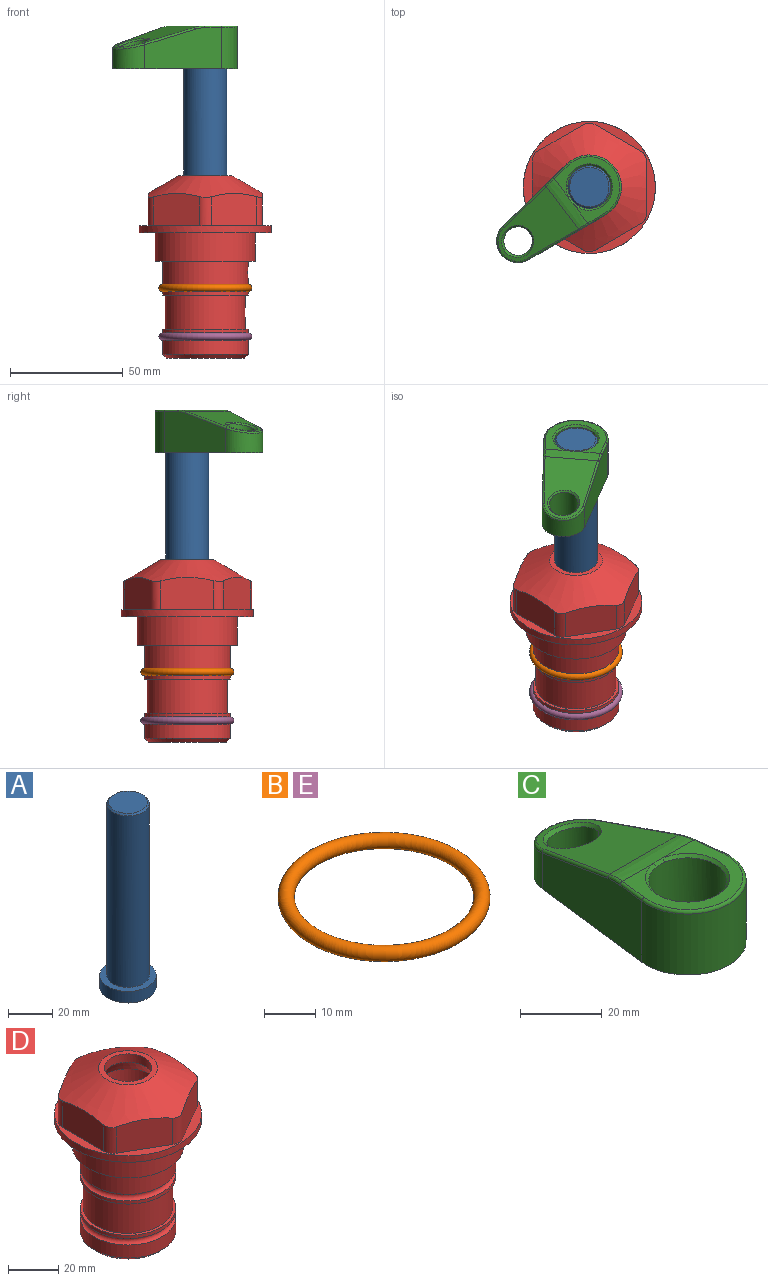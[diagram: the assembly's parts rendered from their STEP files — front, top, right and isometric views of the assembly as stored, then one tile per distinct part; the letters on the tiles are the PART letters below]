
ASSEMBLY  parts=5 mates=4
PART A: 6 faces, bbox 25.4x25.4x101.6 mm
  f0: plane 17.46x17.46mm, normal (0,0,1), area 239.5mm2, adj f5
  f1: plane 25.4x25.4mm, normal (0,0,-1), area 506.7mm2, adj f2
  f2: cylinder r=12.7mm len=25.4mm, axis (0,0,1), area 506.7mm2, adj f1,f3
  f3: plane 25.4x25.4mm, normal (0,0,1), area 221.7mm2, adj f2,f4
  f4: cylinder r=9.53mm len=94.46mm, axis (0,0,1), area 5653mm2, adj f3,f5
  f5: cone r=8.73mm half-angle=45deg, axis (0,0,-1), area 64.4mm2, adj f0,f4
PART B: 1 faces, bbox 44.7x44.7x3.2 mm
  f0: torus R=19.05mm, axis (0,0,1), area 1193.9mm2
PART C: 31 faces, bbox 31.7x65.5x19.8 mm
  f0: plane 39.12x18.26mm, normal (0.99,0.12,0), area 612.2mm2, adj f1,f4,f7,f11,f13,f15
  f1: cylinder r=9.53mm len=18.91mm, axis (0,0,-1), area 296.1mm2, adj f0,f2,f7,f17
  f2: plane 39.12x18.26mm, normal (-0.99,0.12,0), area 612.2mm2, adj f1,f4,f7,f12,f14,f16
  f3: cylinder r=6.35mm len=12.7mm, axis (0,0,-1), area 362.4mm2, adj f7,f18
  f4: cylinder r=14.29mm len=28.58mm, axis (0,0,-1), area 882.2mm2, adj f0,f2,f7,f10
  f5: cylinder r=9.53mm len=19.05mm, axis (0,0,-1), area 1092.6mm2, adj f7,f19,f20
  f6: plane 26.99x23.69mm, normal (0,0,1), area 216.2mm2, adj f9,f10,f11,f12,f19
  f7: plane 63.5x28.58mm, normal (0,0,-1), area 661.8mm2, adj f0,f1,f2,f3,f4,f5,f22,f23
  f8: plane 33.52x23.6mm, normal (0,0.26,0.97), area 486mm2, adj f9,f15,f16,f17,f18
  f9: cylinder r=19.05mm len=24.72mm, axis (1,0,0), area 120.4mm2, adj f6,f8,f13,f14,f20
  f10: torus R=13.49mm, axis (0,0,1), area 59mm2, adj f4,f6,f11,f12
  f11: cylinder r=0.79mm len=8.67mm, axis (0.12,-0.99,0), area 10.8mm2, adj f0,f6,f10,f13
  f12: cylinder r=0.79mm len=8.67mm, axis (0.12,0.99,0), area 10.8mm2, adj f2,f6,f10,f14
  f13: bspline ~4.95x1.42mm, area 6.1mm2, adj f0,f9,f11,f15
  f14: bspline ~4.95x1.42mm, area 6.1mm2, adj f2,f9,f12,f16
  f15: cylinder r=0.79mm len=25.95mm, axis (0.12,-0.96,0.26), area 32.9mm2, adj f0,f8,f13,f17
  f16: cylinder r=0.79mm len=25.95mm, axis (0.12,0.96,-0.26), area 32.9mm2, adj f2,f8,f14,f17
  f17: bspline ~18.91x8.38mm, area 30mm2, adj f1,f8,f15,f16
  f18: bspline ~14.29x14.29mm, area 48.3mm2, adj f3,f8
  f19: cone r=9.53mm half-angle=45deg, axis (0,0,1), area 66.5mm2, adj f5,f6,f20
  f20: bspline ~3.22x0.96mm, area 3.5mm2, adj f5,f9,f19
  f21: plane 2.75x2.72mm, normal (0,0,-1), area 2.9mm2, adj f23,f25,f28
  f22: plane 23.05x15.88mm, normal (-0.99,-0.12,0), area 323.6mm2, adj f7,f25,f26,f27,f28,f29
  f23: plane 23.05x15.88mm, normal (0.99,-0.12,0), area 323.6mm2, adj f7,f21,f25,f27,f28,f30
  f24: cylinder r=9.53mm len=10.69mm, axis (0,0,-1), area 114.7mm2, adj f7,f27,f29,f30
  f25: cylinder r=12.7mm len=20.59mm, axis (0,0,-1), area 381.1mm2, adj f7,f21,f22,f23,f26,f28
  f26: plane 2.75x2.72mm, normal (0,0,-1), area 2.9mm2, adj f22,f25,f28
  f27: plane 19.72x18.37mm, normal (0,-0.26,-0.97), area 291.8mm2, adj f22,f23,f24,f28,f29,f30
  f28: cylinder r=15.88mm len=19.92mm, axis (1,0,0), area 54.8mm2, adj f21,f22,f23,f25,f26,f27
  f29: cylinder r=1.59mm len=11mm, axis (0,0,-1), area 34.7mm2, adj f7,f22,f24,f27
  f30: cylinder r=1.59mm len=11mm, axis (0,0,-1), area 34.7mm2, adj f7,f23,f24,f27
PART D: 36 faces, bbox 58.7x58.7x81 mm
  f0: cylinder r=17.78mm len=35.56mm, axis (0,0,1), area 1670.8mm2, adj f23,f24,f31
  f1: cylinder r=19.05mm len=38.1mm, axis (0,0,1), area 1191.9mm2, adj f26,f27,f30
  f2: plane 58.66x58.66mm, normal (0,0,-1), area 1150.6mm2, adj f3,f28
  f3: cylinder r=29.33mm len=58.66mm, axis (0,0,-1), area 585.1mm2, adj f2,f4
  f4: plane 58.66x58.66mm, normal (0,0,1), area 475.9mm2, adj f3,f5,f6,f7,f8,f9,f10,f11
  f5: plane 20.32x14.34mm, normal (-0.5,0.87,0), area 324.4mm2, adj f4,f15,f16,f17
  f6: plane 20.32x14.34mm, normal (0.5,0.87,0), area 324.4mm2, adj f4,f14,f15,f17
  f7: plane 23.48x14.34mm, normal (1,0,0), area 324.4mm2, adj f4,f13,f14,f17
  f8: plane 20.32x14.34mm, normal (0.5,-0.87,0), area 324.4mm2, adj f4,f12,f13,f17
  f9: plane 20.32x14.34mm, normal (-0.5,-0.87,0), area 324.4mm2, adj f4,f11,f12,f17
  f10: plane 23.48x14.34mm, normal (-1,0,0), area 324.4mm2, adj f4,f11,f16,f17
  f11: cylinder r=5.08mm len=12.85mm, axis (0,0,-1), area 67.2mm2, adj f4,f9,f10,f17
  f12: cylinder r=5.08mm len=12.85mm, axis (0,0,-1), area 67.2mm2, adj f4,f8,f9,f17
  f13: cylinder r=5.08mm len=12.85mm, axis (0,0,-1), area 67.2mm2, adj f4,f7,f8,f17
  f14: cylinder r=5.08mm len=12.85mm, axis (0,0,-1), area 67.2mm2, adj f4,f6,f7,f17
  f15: cylinder r=5.08mm len=12.85mm, axis (0,0,-1), area 67.2mm2, adj f4,f5,f6,f17
  f16: cylinder r=5.08mm len=12.85mm, axis (0,0,-1), area 67.2mm2, adj f4,f5,f10,f17
  f17: cone r=11.73mm half-angle=60deg, axis (0,0,-1), area 2071.8mm2, adj f5,f6,f7,f8,f9,f10,f11,f12
  f18: plane 23.46x23.46mm, normal (0,0,1), area 147.4mm2, adj f17,f35
  f19: plane 34.93x34.93mm, normal (0,0,-1), area 958mm2, adj f29
  f20: cylinder r=19.05mm len=38.1mm, axis (0,0,1), area 760.1mm2, adj f21,f29
  f21: torus R=19.05mm, axis (0,0,1), area 565.3mm2, adj f20,f22
  f22: cylinder r=19.05mm len=38.1mm, axis (0,0,1), area 190mm2, adj f21,f23
  f23: plane 38.1x38.1mm, normal (0,0,1), area 146.9mm2, adj f0,f22
  f24: plane 38.1x38.1mm, normal (0,0,-1), area 146.9mm2, adj f0,f25
  f25: cylinder r=19.05mm len=38.1mm, axis (0,0,1), area 190mm2, adj f24,f26
  f26: torus R=19.05mm, axis (0,0,1), area 565.3mm2, adj f1,f25
  f27: plane 44.45x44.45mm, normal (0,0,-1), area 411.7mm2, adj f1,f28
  f28: cylinder r=22.23mm len=44.45mm, axis (0,0,1), area 1773.5mm2, adj f2,f27
  f29: cone r=19.05mm half-angle=45deg, axis (0,0,1), area 257.5mm2, adj f19,f20
  f30: cylinder r=3.17mm len=6.75mm, axis (-1,0,0), area 128mm2, adj f1,f33
  f31: cylinder r=3.17mm len=6.35mm, axis (-1,0,0), area 102.5mm2, adj f0,f33
  f32: plane 25.4x25.4mm, normal (0,0,1), area 506.7mm2, adj f33
  f33: cylinder r=12.7mm len=66.42mm, axis (0,0,-1), area 5236.2mm2, adj f30,f31,f32,f34
  f34: cone r=9.53mm half-angle=30deg, axis (0,0,-1), area 443.4mm2, adj f33,f35
  f35: cylinder r=9.53mm len=19.05mm, axis (0,0,-1), area 240.9mm2, adj f18,f34
PART E: same geometry as B
PLACE A rot(axis=(0,0,1),127.2deg) t=(0,0,27.55)mm
PLACE B at identity
PLACE C rot(axis=(0,0,1),127.2deg) t=(0,0,28.35)mm
PLACE D at identity fixed
PLACE E t=(0,0,-21.59)mm
MATE cylindrical D.f0 <-> A.f2  axis (0,0,1) through (0,0,-50.55)mm
MATE fastened D.f0 <-> B.f0  axis (0,0,1) through (0,0,-24.51)mm
MATE fastened C.f4 <-> A.f2  axis (0,0,1) through (0,0,91.05)mm
MATE fastened D.f0 <-> E.f0  axis (0,0,1) through (0,0,-46.1)mm
